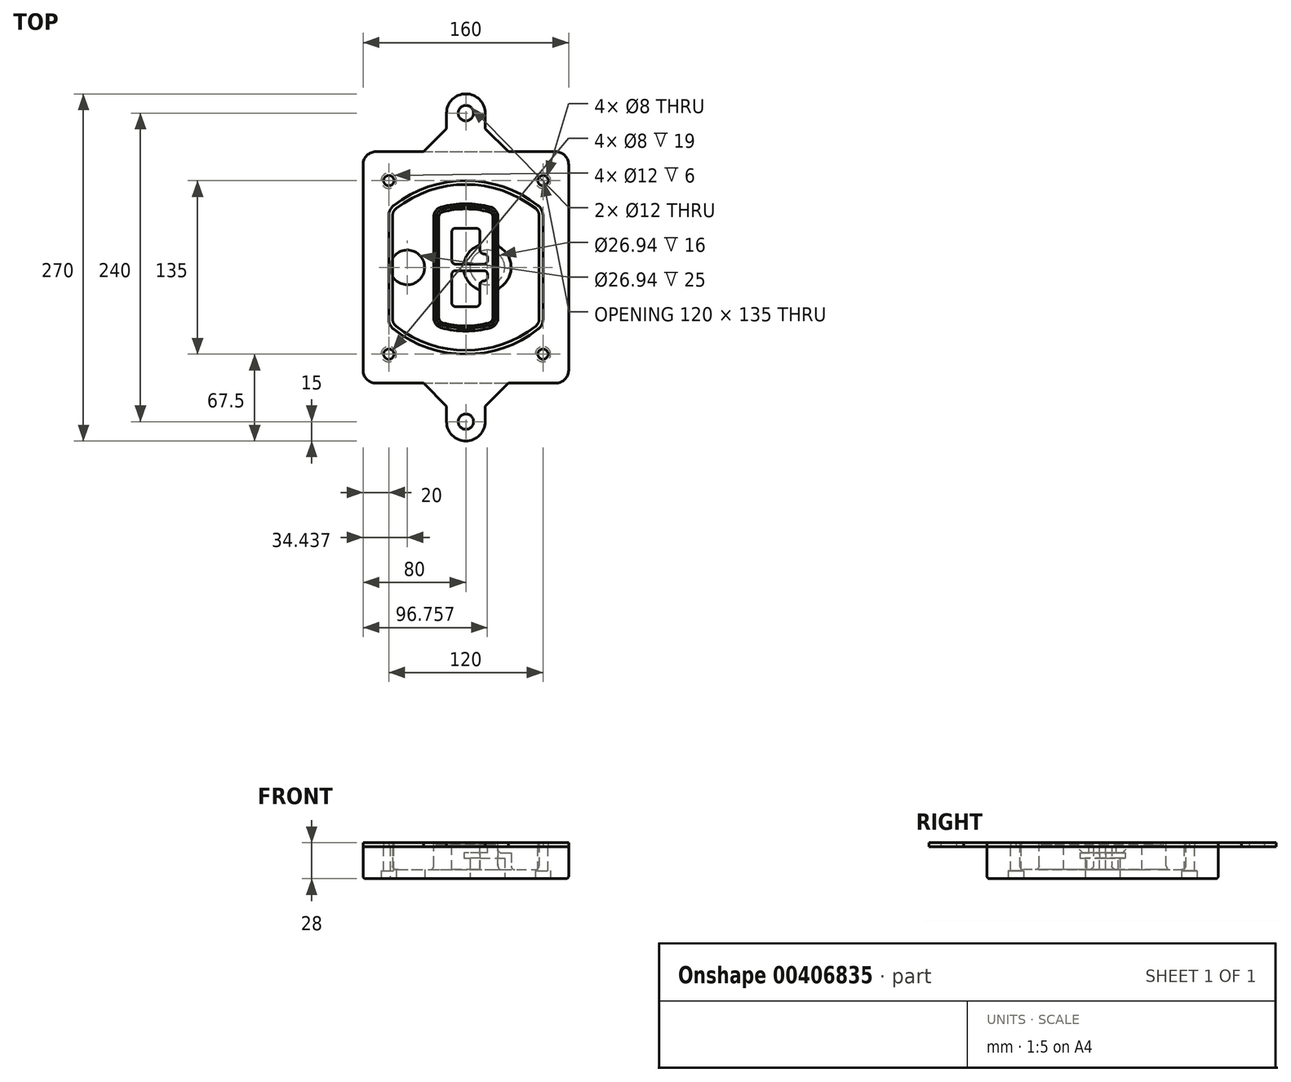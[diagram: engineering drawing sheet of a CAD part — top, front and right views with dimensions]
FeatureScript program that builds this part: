
annotation { "Feature Type Name" : "Feature", "Feature Type Description" : "" }
export const myFeature = defineFeature(function(context is Context, id is Id, definition is map)
    precondition{}
    {
        {
            var Q0;
            Q0=qCreatedBy(makeId("Top.planeOp"),FACE);
            var sketch = newSketch(context, id + "F0", { "sketchPlane" : qUnion([Q0])});
            skPoint(sketch, "E0.rect.middle", {"position": v(0, 0) * mm});
            skLineSegment(sketch, "E1.bottom", {"start": v(-70, -90) * mm, "end": v(70, -90) * mm});
            skLineSegment(sketch, "E1.top", {"start": v(-70, 90) * mm, "end": v(70, 90) * mm});
            skLineSegment(sketch, "E1.left", {"start": v(-80, -80) * mm, "end": v(-80, 80) * mm});
            skLineSegment(sketch, "E1.right", {"start": v(80, -80) * mm, "end": v(80, 80) * mm});
            skLineSegment(sketch, "E2", {"start": v(-80, 90) * mm, "end": v(80, -90) * mm, "construction": true});
            skLineSegment(sketch, "E3", {"start": v(80, 90) * mm, "end": v(-80, -90) * mm, "construction": true});
            skCircle(sketch, "E4", {"center": v(-60, 67.5) * mm, "radius": 4 * mm});
            skCircle(sketch, "E5", {"center": v(60, 67.5) * mm, "radius": 4 * mm});
            skCircle(sketch, "E6", {"center": v(60, -67.5) * mm, "radius": 4 * mm});
            skCircle(sketch, "E7", {"center": v(-60, -67.5) * mm, "radius": 4 * mm});
            skLineSegment(sketch, "E8", {"start": v(-60, 67.5) * mm, "end": v(60, 67.5) * mm, "construction": true});
            skLineSegment(sketch, "E9", {"start": v(60, 67.5) * mm, "end": v(60, -67.5) * mm, "construction": true});
            skLineSegment(sketch, "E10", {"start": v(60, -67.5) * mm, "end": v(-60, -67.5) * mm, "construction": true});
            skLineSegment(sketch, "E11", {"start": v(-60, -67.5) * mm, "end": v(-60, 67.5) * mm, "construction": true});
            skLineSegment(sketch, "E12", {"start": v(-60, 40.3) * mm, "end": v(-60, -40.3) * mm});
            skLineSegment(sketch, "E13", {"start": v(60, 40.3) * mm, "end": v(60, -40.3) * mm});
            skArc(sketch, "E14", {"start": v(56.15, 48.18) * mm, "mid": v(0, 67.5) * mm, "end": v(-56.15, 48.18) * mm});
            skArc(sketch, "E15", {"start": v(-56.15, -48.18) * mm, "mid": v(0, -67.5) * mm, "end": v(56.15, -48.18) * mm});
            skLineSegment(sketch, "E16", {"start": v(-60, 0) * mm, "end": v(60, 0) * mm, "construction": true});
            skPoint(sketch, "E17.visualSharp", {"position": v(-60, -45) * mm});
            skArc(sketch, "E17.filletArc", {"start": v(-60, -40.3) * mm, "mid": v(-58.99, -44.68) * mm, "end": v(-56.15, -48.18) * mm});
            skPoint(sketch, "E18.visualSharp", {"position": v(-60, 45) * mm});
            skArc(sketch, "E18.filletArc", {"start": v(-56.15, 48.18) * mm, "mid": v(-58.99, 44.68) * mm, "end": v(-60, 40.3) * mm});
            skPoint(sketch, "E19.visualSharp", {"position": v(60, 45) * mm});
            skArc(sketch, "E19.filletArc", {"start": v(60, 40.3) * mm, "mid": v(58.99, 44.68) * mm, "end": v(56.15, 48.18) * mm});
            skPoint(sketch, "E20.visualSharp", {"position": v(60, -45) * mm});
            skArc(sketch, "E20.filletArc", {"start": v(56.15, -48.18) * mm, "mid": v(58.99, -44.68) * mm, "end": v(60, -40.3) * mm});
            skPoint(sketch, "E21.visualSharp", {"position": v(-80, 90) * mm});
            skArc(sketch, "E21.filletArc", {"start": v(-70, 90) * mm, "mid": v(-77.07, 87.07) * mm, "end": v(-80, 80) * mm});
            skPoint(sketch, "E22.visualSharp", {"position": v(80, 90) * mm});
            skArc(sketch, "E22.filletArc", {"start": v(80, 80) * mm, "mid": v(77.07, 87.07) * mm, "end": v(70, 90) * mm});
            skPoint(sketch, "E23.visualSharp", {"position": v(80, -90) * mm});
            skArc(sketch, "E23.filletArc", {"start": v(70, -90) * mm, "mid": v(77.07, -87.07) * mm, "end": v(80, -80) * mm});
            skPoint(sketch, "E24.visualSharp", {"position": v(-80, -90) * mm});
            skArc(sketch, "E24.filletArc", {"start": v(-80, -80) * mm, "mid": v(-77.07, -87.07) * mm, "end": v(-70, -90) * mm});
            skArc(sketch, "E25.0", {"start": v(57, 40.3) * mm, "mid": v(56.3, 43.36) * mm, "end": v(54.3, 45.81) * mm});
            skLineSegment(sketch, "E25.1", {"start": v(57, 40.3) * mm, "end": v(57, -40.3) * mm});
            skArc(sketch, "E25.2", {"start": v(54.3, -45.81) * mm, "mid": v(56.3, -43.36) * mm, "end": v(57, -40.3) * mm});
            skArc(sketch, "E25.3", {"start": v(-54.3, -45.81) * mm, "mid": v(0, -64.5) * mm, "end": v(54.3, -45.81) * mm});
            skArc(sketch, "E25.4", {"start": v(-57, -40.3) * mm, "mid": v(-56.3, -43.36) * mm, "end": v(-54.3, -45.81) * mm});
            skArc(sketch, "E25.5", {"start": v(54.3, 45.81) * mm, "mid": v(0, 64.5) * mm, "end": v(-54.3, 45.81) * mm});
            skLineSegment(sketch, "E25.6", {"start": v(-57, 40.3) * mm, "end": v(-57, -40.3) * mm});
            skArc(sketch, "E25.7", {"start": v(-54.3, 45.81) * mm, "mid": v(-56.3, 43.36) * mm, "end": v(-57, 40.3) * mm});
            skArc(sketch, "E26.0", {"start": v(-58.62, 51.33) * mm, "mid": v(-62.58, 46.43) * mm, "end": v(-64, 40.3) * mm});
            skArc(sketch, "E26.1", {"start": v(58.62, 51.33) * mm, "mid": v(0, 71.5) * mm, "end": v(-58.62, 51.33) * mm});
            skArc(sketch, "E26.2", {"start": v(64, 40.3) * mm, "mid": v(62.58, 46.43) * mm, "end": v(58.62, 51.33) * mm});
            skLineSegment(sketch, "E26.3", {"start": v(64, 40.3) * mm, "end": v(64, -40.3) * mm});
            skArc(sketch, "E26.4", {"start": v(58.62, -51.33) * mm, "mid": v(62.58, -46.43) * mm, "end": v(64, -40.3) * mm});
            skLineSegment(sketch, "E26.5", {"start": v(-64, 40.3) * mm, "end": v(-64, -40.3) * mm});
            skArc(sketch, "E26.6", {"start": v(-58.62, -51.33) * mm, "mid": v(0, -71.5) * mm, "end": v(58.62, -51.33) * mm});
            skArc(sketch, "E26.7", {"start": v(-64, -40.3) * mm, "mid": v(-62.58, -46.43) * mm, "end": v(-58.62, -51.33) * mm});
            skSolve(sketch);
        }
        {
            var Q0;
            Q0=makeQuery(id+"F0.imprint","IMPRINT",FACE,{"disambiguationData":[TD([[makeQuery(id+"F0.imprint","IMPRINT",EDGE,{"derivedFrom":sQuery(id+"F0.wireOp",EDGE,"E1.bottom")}),1.0]])]});
            var Q1;
            Q1=makeQuery(id+"F0.imprint","IMPRINT",FACE,{"disambiguationData":[TD([[makeQuery(id+"F0.imprint","IMPRINT",EDGE,{"derivedFrom":sQuery(id+"F0.wireOp",EDGE,"E12")}),1.0]])]});
            var Q2;
            Q2=makeQuery(id+"F0.imprint","IMPRINT",FACE,{"disambiguationData":[TD([[makeQuery(id+"F0.imprint","IMPRINT",EDGE,{"derivedFrom":sQuery(id+"F0.wireOp",EDGE,"E25.0")}),1.0]])]});
            var Q3;
            Q3=makeQuery(id+"F0.imprint","IMPRINT",FACE,{"disambiguationData":[TD([[makeQuery(id+"F0.imprint","IMPRINT",EDGE,{"derivedFrom":sQuery(id+"F0.wireOp",EDGE,"E12")}),-1.0]])]});
            extrude(context, id + "F1", {"entities" : qUnion([Q0, Q1, Q2, Q3]), "oppositeDirection" : true, "depth" : 25 * mm});
        }
        {
            var Q0;
            Q0=makeQuery(id+"F0.imprint","IMPRINT",FACE,{"disambiguationData":[TD([[makeQuery(id+"F0.imprint","IMPRINT",EDGE,{"derivedFrom":sQuery(id+"F0.wireOp",EDGE,"E12")}),1.0]])]});
            extrude(context, id + "F2", {"entities" : qUnion([Q0]), "operationType" : NewBodyOperationType.ADD, "depth" : 3 * mm});
        }
        {
            var Q0;
            Q0=makeQuery(id+"F0.imprint","IMPRINT",FACE,{"disambiguationData":[TD([[makeQuery(id+"F0.imprint","IMPRINT",EDGE,{"derivedFrom":sQuery(id+"F0.wireOp",EDGE,"E25.0")}),1.0]])]});
            extrude(context, id + "F3", {"entities" : qUnion([Q0]), "operationType" : NewBodyOperationType.REMOVE, "oppositeDirection" : true, "depth" : 18 * mm});
        }
        {
            var Q0;
            Q0=makeQuery(id+"F2.opExtrude","CAP_FACE",FACE,{"disambiguationData":[OSD([sQuery(id+"F0.wireOp",EDGE,"E12"),sQuery(id+"F0.wireOp",EDGE,"E13"),sQuery(id+"F0.wireOp",EDGE,"E14"),sQuery(id+"F0.wireOp",EDGE,"E15"),sQuery(id+"F0.wireOp",EDGE,"E17.filletArc"),sQuery(id+"F0.wireOp",EDGE,"E18.filletArc"),sQuery(id+"F0.wireOp",EDGE,"E19.filletArc"),sQuery(id+"F0.wireOp",EDGE,"E20.filletArc"),sQuery(id+"F0.wireOp",EDGE,"E25.0"),sQuery(id+"F0.wireOp",EDGE,"E25.1"),sQuery(id+"F0.wireOp",EDGE,"E25.2"),sQuery(id+"F0.wireOp",EDGE,"E25.3"),sQuery(id+"F0.wireOp",EDGE,"E25.4"),sQuery(id+"F0.wireOp",EDGE,"E25.5"),sQuery(id+"F0.wireOp",EDGE,"E25.6"),sQuery(id+"F0.wireOp",EDGE,"E25.7")])],"isStart":false});
            var sketch = newSketch(context, id + "F4", { "sketchPlane" : qUnion([Q0])});
            skArc(sketch, "E27.0", {"start": v(-19.08, -46.97) * mm, "mid": v(0, -49.5) * mm, "end": v(19.08, -46.97) * mm});
            skArc(sketch, "E28.0", {"start": v(19.08, 46.97) * mm, "mid": v(0, 49.5) * mm, "end": v(-19.08, 46.97) * mm});
            skLineSegment(sketch, "E29", {"start": v(-25, 39.25) * mm, "end": v(-25, -39.25) * mm});
            skLineSegment(sketch, "E30", {"start": v(25, 39.25) * mm, "end": v(25, -39.25) * mm});
            skLineSegment(sketch, "E31", {"start": v(-25, 45.1) * mm, "end": v(25, 45.1) * mm, "construction": true});
            skLineSegment(sketch, "E32", {"start": v(-25, -45.1) * mm, "end": v(25, -45.1) * mm, "construction": true});
            skPoint(sketch, "E33.visualSharp", {"position": v(-25, 45.1) * mm});
            skArc(sketch, "E33.filletArc", {"start": v(-19.08, 46.97) * mm, "mid": v(-23.35, 44.11) * mm, "end": v(-25, 39.25) * mm});
            skPoint(sketch, "E34.visualSharp", {"position": v(25, 45.1) * mm});
            skArc(sketch, "E34.filletArc", {"start": v(25, 39.25) * mm, "mid": v(23.35, 44.11) * mm, "end": v(19.08, 46.97) * mm});
            skPoint(sketch, "E35.visualSharp", {"position": v(25, -45.1) * mm});
            skArc(sketch, "E35.filletArc", {"start": v(19.08, -46.97) * mm, "mid": v(23.35, -44.11) * mm, "end": v(25, -39.25) * mm});
            skPoint(sketch, "E36.visualSharp", {"position": v(-25, -45.1) * mm});
            skArc(sketch, "E36.filletArc", {"start": v(-25, -39.25) * mm, "mid": v(-23.35, -44.11) * mm, "end": v(-19.08, -46.97) * mm});
            skArc(sketch, "E37.0", {"start": v(54.3, 45.81) * mm, "mid": v(0, 64.5) * mm, "end": v(-54.3, 45.81) * mm});
            skArc(sketch, "E37.1", {"start": v(-54.3, 45.81) * mm, "mid": v(-56.3, 43.36) * mm, "end": v(-57, 40.3) * mm});
            skLineSegment(sketch, "E37.2", {"start": v(-57, 40.3) * mm, "end": v(-57, -40.3) * mm});
            skArc(sketch, "E37.3", {"start": v(-57, -40.3) * mm, "mid": v(-56.3, -43.36) * mm, "end": v(-54.3, -45.81) * mm});
            skArc(sketch, "E37.4", {"start": v(-54.3, -45.81) * mm, "mid": v(0, -64.5) * mm, "end": v(54.3, -45.81) * mm});
            skArc(sketch, "E37.5", {"start": v(54.3, -45.81) * mm, "mid": v(56.3, -43.36) * mm, "end": v(57, -40.3) * mm});
            skLineSegment(sketch, "E37.6", {"start": v(57, 40.3) * mm, "end": v(57, -40.3) * mm});
            skArc(sketch, "E37.7", {"start": v(57, 40.3) * mm, "mid": v(56.3, 43.36) * mm, "end": v(54.3, 45.81) * mm});
            skLineSegment(sketch, "E38.0", {"start": v(23, 39.25) * mm, "end": v(23, -39.25) * mm});
            skArc(sketch, "E38.1", {"start": v(18.56, -45.04) * mm, "mid": v(21.76, -42.9) * mm, "end": v(23, -39.25) * mm});
            skArc(sketch, "E38.2", {"start": v(-18.56, -45.04) * mm, "mid": v(0, -47.5) * mm, "end": v(18.56, -45.04) * mm});
            skArc(sketch, "E38.3", {"start": v(-23, -39.25) * mm, "mid": v(-21.76, -42.9) * mm, "end": v(-18.56, -45.04) * mm});
            skLineSegment(sketch, "E38.4", {"start": v(-23, 39.25) * mm, "end": v(-23, -39.25) * mm});
            skArc(sketch, "E38.5", {"start": v(23, 39.25) * mm, "mid": v(21.76, 42.9) * mm, "end": v(18.56, 45.04) * mm});
            skArc(sketch, "E38.6", {"start": v(-18.56, 45.04) * mm, "mid": v(-21.76, 42.9) * mm, "end": v(-23, 39.25) * mm});
            skArc(sketch, "E38.7", {"start": v(18.56, 45.04) * mm, "mid": v(0, 47.5) * mm, "end": v(-18.56, 45.04) * mm});
            skArc(sketch, "E39.0", {"start": v(21, 39.25) * mm, "mid": v(20.18, 41.68) * mm, "end": v(18.04, 43.1) * mm});
            skLineSegment(sketch, "E39.1", {"start": v(21, 39.25) * mm, "end": v(21, -39.25) * mm});
            skArc(sketch, "E39.2", {"start": v(18.04, -43.1) * mm, "mid": v(20.18, -41.68) * mm, "end": v(21, -39.25) * mm});
            skArc(sketch, "E39.3", {"start": v(-18.04, -43.1) * mm, "mid": v(0, -45.5) * mm, "end": v(18.04, -43.1) * mm});
            skArc(sketch, "E39.4", {"start": v(-21, -39.25) * mm, "mid": v(-20.18, -41.68) * mm, "end": v(-18.04, -43.1) * mm});
            skArc(sketch, "E39.5", {"start": v(18.04, 43.1) * mm, "mid": v(0, 45.5) * mm, "end": v(-18.04, 43.1) * mm});
            skLineSegment(sketch, "E39.6", {"start": v(-21, 39.25) * mm, "end": v(-21, -39.25) * mm});
            skArc(sketch, "E39.7", {"start": v(-18.04, 43.1) * mm, "mid": v(-20.18, 41.68) * mm, "end": v(-21, 39.25) * mm});
            skLineSegment(sketch, "E40", {"start": v(-25, 0) * mm, "end": v(25, 0) * mm, "construction": true});
            skLineSegment(sketch, "E41", {"start": v(-11, 5.5) * mm, "end": v(-11, 27.5) * mm});
            skLineSegment(sketch, "E42", {"start": v(-8, 30.5) * mm, "end": v(8, 30.5) * mm});
            skLineSegment(sketch, "E43", {"start": v(11, 27.5) * mm, "end": v(11, 13.5) * mm});
            skLineSegment(sketch, "E44", {"start": v(14, 10.5) * mm, "end": v(14, 10.5) * mm});
            skLineSegment(sketch, "E45", {"start": v(17, 7.5) * mm, "end": v(17, 5.5) * mm});
            skLineSegment(sketch, "E46", {"start": v(14, 2.5) * mm, "end": v(-8, 2.5) * mm});
            skPoint(sketch, "E47.visualSharp", {"position": v(-11, 30.5) * mm});
            skArc(sketch, "E47.filletArc", {"start": v(-8, 30.5) * mm, "mid": v(-10.12, 29.62) * mm, "end": v(-11, 27.5) * mm});
            skPoint(sketch, "E48.visualSharp", {"position": v(11, 30.5) * mm});
            skArc(sketch, "E48.filletArc", {"start": v(11, 27.5) * mm, "mid": v(10.12, 29.62) * mm, "end": v(8, 30.5) * mm});
            skPoint(sketch, "E49.visualSharp", {"position": v(11, 10.5) * mm});
            skArc(sketch, "E49.filletArc", {"start": v(11, 13.5) * mm, "mid": v(11.88, 11.38) * mm, "end": v(14, 10.5) * mm});
            skPoint(sketch, "E50.visualSharp", {"position": v(17, 10.5) * mm});
            skArc(sketch, "E50.filletArc", {"start": v(17, 7.5) * mm, "mid": v(16.12, 9.62) * mm, "end": v(14, 10.5) * mm});
            skPoint(sketch, "E51.visualSharp", {"position": v(17, 2.5) * mm});
            skArc(sketch, "E51.filletArc", {"start": v(14, 2.5) * mm, "mid": v(16.12, 3.38) * mm, "end": v(17, 5.5) * mm});
            skPoint(sketch, "E52.visualSharp", {"position": v(-11, 2.5) * mm});
            skArc(sketch, "E52.filletArc", {"start": v(-11, 5.5) * mm, "mid": v(-10.12, 3.38) * mm, "end": v(-8, 2.5) * mm});
            skLineSegment(sketch, "E53.0.MirrorCS", {"start": v(14, -2.5) * mm, "end": v(-8, -2.5) * mm});
            skArc(sketch, "E54.0.MirrorCS", {"start": v(-11, -5.5) * mm, "mid": v(-10.12, -3.38) * mm, "end": v(-8, -2.5) * mm});
            skLineSegment(sketch, "E55.0.MirrorCS", {"start": v(-11, -5.5) * mm, "end": v(-11, -27.5) * mm});
            skArc(sketch, "E56.0.MirrorCS", {"start": v(-8, -30.5) * mm, "mid": v(-10.12, -29.62) * mm, "end": v(-11, -27.5) * mm});
            skLineSegment(sketch, "E57.0.MirrorCS", {"start": v(-8, -30.5) * mm, "end": v(8, -30.5) * mm});
            skArc(sketch, "E58.0.MirrorCS", {"start": v(11, -27.5) * mm, "mid": v(10.12, -29.62) * mm, "end": v(8, -30.5) * mm});
            skLineSegment(sketch, "E59.0.MirrorCS", {"start": v(11, -27.5) * mm, "end": v(11, -13.5) * mm});
            skArc(sketch, "E60.0.MirrorCS", {"start": v(11, -13.5) * mm, "mid": v(11.88, -11.38) * mm, "end": v(14, -10.5) * mm});
            skArc(sketch, "E61.0.MirrorCS", {"start": v(17, -7.5) * mm, "mid": v(16.12, -9.62) * mm, "end": v(14, -10.5) * mm});
            skLineSegment(sketch, "E62.0.MirrorCS", {"start": v(17, -7.5) * mm, "end": v(17, -5.5) * mm});
            skArc(sketch, "E63.0.MirrorCS", {"start": v(14, -2.5) * mm, "mid": v(16.12, -3.38) * mm, "end": v(17, -5.5) * mm});
            skSolve(sketch);
        }
        {
            var Q0;
            Q0=makeQuery(id+"F4.imprint","IMPRINT",FACE,{"disambiguationData":[TD([[makeQuery(id+"F4.imprint","IMPRINT",EDGE,{"derivedFrom":sQuery(id+"F4.wireOp",EDGE,"E27.0")}),1.0]])]});
            var Q1;
            Q1=makeQuery(id+"F4.imprint","IMPRINT",FACE,{"disambiguationData":[TD([[makeQuery(id+"F4.imprint","IMPRINT",EDGE,{"derivedFrom":sQuery(id+"F4.wireOp",EDGE,"E38.0")}),-1.0]])]});
            var Q2;
            Q2=makeQuery(id+"F4.imprint","IMPRINT",FACE,{"disambiguationData":[TD([[makeQuery(id+"F4.imprint","IMPRINT",EDGE,{"derivedFrom":sQuery(id+"F4.wireOp",EDGE,"E39.0")}),1.0]])]});
            extrude(context, id + "F5", {"entities" : qUnion([Q0, Q1, Q2]), "operationType" : NewBodyOperationType.ADD, "endBound" : BoundingType.UP_TO_NEXT, "oppositeDirection" : true, "depth" : 25 * mm});
        }
        {
            var Q0;
            Q0=makeQuery(id+"F4.imprint","IMPRINT",FACE,{"disambiguationData":[TD([[makeQuery(id+"F4.imprint","IMPRINT",EDGE,{"derivedFrom":sQuery(id+"F4.wireOp",EDGE,"E38.0")}),-1.0]])]});
            extrude(context, id + "F6", {"entities" : qUnion([Q0]), "operationType" : NewBodyOperationType.REMOVE, "oppositeDirection" : true, "depth" : 2 * mm});
        }
        {
            var Q0;
            Q0=makeQuery(id+"F1.opExtrude","CAP_FACE",FACE,{"disambiguationData":[OSD([sQuery(id+"F0.wireOp",EDGE,"E1.bottom"),sQuery(id+"F0.wireOp",EDGE,"E1.top"),sQuery(id+"F0.wireOp",EDGE,"E1.left"),sQuery(id+"F0.wireOp",EDGE,"E1.right"),sQuery(id+"F0.wireOp",EDGE,"E4"),sQuery(id+"F0.wireOp",EDGE,"E5"),sQuery(id+"F0.wireOp",EDGE,"E6"),sQuery(id+"F0.wireOp",EDGE,"E7"),sQuery(id+"F0.wireOp",EDGE,"E21.filletArc"),sQuery(id+"F0.wireOp",EDGE,"E22.filletArc"),sQuery(id+"F0.wireOp",EDGE,"E23.filletArc"),sQuery(id+"F0.wireOp",EDGE,"E24.filletArc")])],"isStart":false});
            var sketch = newSketch(context, id + "F7", { "sketchPlane" : qUnion([Q0])});
            skCircle(sketch, "E64", {"center": v(16.76, 0) * mm, "radius": 13.47 * mm});
            skCircle(sketch, "E65", {"center": v(-45.56, 0) * mm, "radius": 13.47 * mm});
            skLineSegment(sketch, "E66", {"start": v(80, 0) * mm, "end": v(-80, 0) * mm});
            skCircle(sketch, "E67", {"center": v(16.76, 0) * mm, "radius": 18.47 * mm});
            skCircle(sketch, "E68", {"center": v(60, -67.5) * mm, "radius": 6 * mm});
            skCircle(sketch, "E69", {"center": v(-60, -67.5) * mm, "radius": 6 * mm});
            skCircle(sketch, "E70", {"center": v(-60, 67.5) * mm, "radius": 6 * mm});
            skCircle(sketch, "E71", {"center": v(60, 67.5) * mm, "radius": 6 * mm});
            skSolve(sketch);
        }
        {
            var Q0;
            {var subQ1=sQuery(id+"F7.wireOp",EDGE,"E66");var subQ4=sQuery(id+"F7.wireOp",EDGE,"E64");var subQ6=makeQuery(id+"F7.imprint","INTERSECT",VERTEX,{"disambiguationData":[OD(0.0)],"derivedFrom":[subQ4,subQ1]});Q0=makeQuery(id+"F7.imprint","IMPRINT",FACE,{"disambiguationData":[TD([[makeQuery(id+"F7.imprint","IMPRINT",EDGE,{"disambiguationData":[TD([[subQ6,-1.0]])],"derivedFrom":subQ4}),-1.0]])]});}
            var Q1;
            {var subQ0=sQuery(id+"F7.wireOp",EDGE,"E66");var subQ1=sQuery(id+"F7.wireOp",EDGE,"E64");var subQ3=makeQuery(id+"F7.imprint","INTERSECT",VERTEX,{"disambiguationData":[OD(0.0)],"derivedFrom":[subQ1,subQ0]});Q1=makeQuery(id+"F7.imprint","IMPRINT",FACE,{"disambiguationData":[TD([[makeQuery(id+"F7.imprint","IMPRINT",EDGE,{"disambiguationData":[TD([[subQ3,-1.0]])],"derivedFrom":subQ1}),1.0]])]});}
            var Q2;
            {var subQ0=sQuery(id+"F7.wireOp",EDGE,"E66");var subQ1=sQuery(id+"F7.wireOp",EDGE,"E64");var subQ3=makeQuery(id+"F7.imprint","INTERSECT",VERTEX,{"disambiguationData":[OD(0.0)],"derivedFrom":[subQ1,subQ0]});Q2=makeQuery(id+"F7.imprint","IMPRINT",FACE,{"disambiguationData":[TD([[makeQuery(id+"F7.imprint","IMPRINT",EDGE,{"disambiguationData":[TD([[subQ3,1.0]])],"derivedFrom":subQ1}),1.0]])]});}
            var Q3;
            {var subQ1=sQuery(id+"F7.wireOp",EDGE,"E66");var subQ4=sQuery(id+"F7.wireOp",EDGE,"E64");var subQ6=makeQuery(id+"F7.imprint","INTERSECT",VERTEX,{"disambiguationData":[OD(0.0)],"derivedFrom":[subQ4,subQ1]});Q3=makeQuery(id+"F7.imprint","IMPRINT",FACE,{"disambiguationData":[TD([[makeQuery(id+"F7.imprint","IMPRINT",EDGE,{"disambiguationData":[TD([[subQ6,1.0]])],"derivedFrom":subQ4}),-1.0]])]});}
            extrude(context, id + "F8", {"entities" : qUnion([Q0, Q1, Q2, Q3]), "operationType" : NewBodyOperationType.ADD, "oppositeDirection" : true, "depth" : 20 * mm});
        }
        {
            var Q0;
            {var subQ0=sQuery(id+"F7.wireOp",EDGE,"E66");var subQ1=sQuery(id+"F7.wireOp",EDGE,"E64");var subQ3=makeQuery(id+"F7.imprint","INTERSECT",VERTEX,{"disambiguationData":[OD(0.0)],"derivedFrom":[subQ1,subQ0]});Q0=makeQuery(id+"F7.imprint","IMPRINT",FACE,{"disambiguationData":[TD([[makeQuery(id+"F7.imprint","IMPRINT",EDGE,{"disambiguationData":[TD([[subQ3,-1.0]])],"derivedFrom":subQ1}),1.0]])]});}
            var Q1;
            {var subQ0=sQuery(id+"F7.wireOp",EDGE,"E66");var subQ1=sQuery(id+"F7.wireOp",EDGE,"E64");var subQ3=makeQuery(id+"F7.imprint","INTERSECT",VERTEX,{"disambiguationData":[OD(0.0)],"derivedFrom":[subQ1,subQ0]});Q1=makeQuery(id+"F7.imprint","IMPRINT",FACE,{"disambiguationData":[TD([[makeQuery(id+"F7.imprint","IMPRINT",EDGE,{"disambiguationData":[TD([[subQ3,1.0]])],"derivedFrom":subQ1}),1.0]])]});}
            extrude(context, id + "F9", {"entities" : qUnion([Q0, Q1]), "operationType" : NewBodyOperationType.REMOVE, "oppositeDirection" : true, "depth" : 16 * mm});
        }
        {
            var Q0;
            {var subQ0=sQuery(id+"F7.wireOp",EDGE,"E66");var subQ1=sQuery(id+"F7.wireOp",EDGE,"E65");var subQ3=makeQuery(id+"F7.imprint","INTERSECT",VERTEX,{"disambiguationData":[OD(0.0)],"derivedFrom":[subQ1,subQ0]});Q0=makeQuery(id+"F7.imprint","IMPRINT",FACE,{"disambiguationData":[TD([[makeQuery(id+"F7.imprint","IMPRINT",EDGE,{"disambiguationData":[TD([[subQ3,-1.0]])],"derivedFrom":subQ1}),1.0]])]});}
            var Q1;
            {var subQ0=sQuery(id+"F7.wireOp",EDGE,"E66");var subQ1=sQuery(id+"F7.wireOp",EDGE,"E65");var subQ3=makeQuery(id+"F7.imprint","INTERSECT",VERTEX,{"disambiguationData":[OD(0.0)],"derivedFrom":[subQ1,subQ0]});Q1=makeQuery(id+"F7.imprint","IMPRINT",FACE,{"disambiguationData":[TD([[makeQuery(id+"F7.imprint","IMPRINT",EDGE,{"disambiguationData":[TD([[subQ3,1.0]])],"derivedFrom":subQ1}),1.0]])]});}
            extrude(context, id + "F10", {"entities" : qUnion([Q0, Q1]), "operationType" : NewBodyOperationType.REMOVE, "oppositeDirection" : true, "depth" : 25 * mm});
        }
        {
            var Q0;
            Q0=makeQuery(id+"F7.imprint","IMPRINT",FACE,{"disambiguationData":[TD([[makeQuery(id+"F7.imprint","IMPRINT",EDGE,{"derivedFrom":sQuery(id+"F7.wireOp",EDGE,"E68")}),1.0]])]});
            var Q1;
            Q1=makeQuery(id+"F7.imprint","IMPRINT",FACE,{"disambiguationData":[TD([[makeQuery(id+"F7.imprint","IMPRINT",EDGE,{"derivedFrom":makeQuery(id+"F1.opExtrude","CAP_EDGE",EDGE,{"disambiguationData":[OSD([sQuery(id+"F0.wireOp",EDGE,"E5")])],"isStart":false})}),-1.0]])]});
            var Q2;
            Q2=makeQuery(id+"F7.imprint","IMPRINT",FACE,{"disambiguationData":[TD([[makeQuery(id+"F7.imprint","IMPRINT",EDGE,{"derivedFrom":sQuery(id+"F7.wireOp",EDGE,"E69")}),1.0]])]});
            var Q3;
            Q3=makeQuery(id+"F7.imprint","IMPRINT",FACE,{"disambiguationData":[TD([[makeQuery(id+"F7.imprint","IMPRINT",EDGE,{"derivedFrom":makeQuery(id+"F1.opExtrude","CAP_EDGE",EDGE,{"disambiguationData":[OSD([sQuery(id+"F0.wireOp",EDGE,"E4")])],"isStart":false})}),-1.0]])]});
            var Q4;
            Q4=makeQuery(id+"F7.imprint","IMPRINT",FACE,{"disambiguationData":[TD([[makeQuery(id+"F7.imprint","IMPRINT",EDGE,{"derivedFrom":sQuery(id+"F7.wireOp",EDGE,"E70")}),1.0]])]});
            var Q5;
            Q5=makeQuery(id+"F7.imprint","IMPRINT",FACE,{"disambiguationData":[TD([[makeQuery(id+"F7.imprint","IMPRINT",EDGE,{"derivedFrom":makeQuery(id+"F1.opExtrude","CAP_EDGE",EDGE,{"disambiguationData":[OSD([sQuery(id+"F0.wireOp",EDGE,"E7")])],"isStart":false})}),-1.0]])]});
            var Q6;
            Q6=makeQuery(id+"F7.imprint","IMPRINT",FACE,{"disambiguationData":[TD([[makeQuery(id+"F7.imprint","IMPRINT",EDGE,{"derivedFrom":sQuery(id+"F7.wireOp",EDGE,"E71")}),1.0]])]});
            var Q7;
            Q7=makeQuery(id+"F7.imprint","IMPRINT",FACE,{"disambiguationData":[TD([[makeQuery(id+"F7.imprint","IMPRINT",EDGE,{"derivedFrom":makeQuery(id+"F1.opExtrude","CAP_EDGE",EDGE,{"disambiguationData":[OSD([sQuery(id+"F0.wireOp",EDGE,"E6")])],"isStart":false})}),-1.0]])]});
            extrude(context, id + "F11", {"entities" : qUnion([Q0, Q1, Q2, Q3, Q4, Q5, Q6, Q7]), "operationType" : NewBodyOperationType.REMOVE, "oppositeDirection" : true, "depth" : 6 * mm});
        }
        {
            var Q0;
            Q0=makeQuery(id+"F9.boolean.opBoolean","COPY",FACE,{"derivedFrom":makeQuery(id+"F9.opExtrude","CAP_FACE",FACE,{"disambiguationData":[OSD([sQuery(id+"F7.wireOp",EDGE,"E64")])],"isStart":false})});
            var sketch = newSketch(context, id + "F12", { "sketchPlane" : qUnion([Q0])});
            skArc(sketch, "E72.0", {"start": v(11, 17.55) * mm, "mid": v(2.57, 11.82) * mm, "end": v(-1.54, 2.5) * mm});
            skArc(sketch, "E72.1", {"start": v(-1.54, -2.5) * mm, "mid": v(2.57, -11.82) * mm, "end": v(11, -17.55) * mm});
            skLineSegment(sketch, "E73", {"start": v(-1.54, -2.5) * mm, "end": v(14, -2.5) * mm});
            skLineSegment(sketch, "E74.0", {"start": v(14, 2.5) * mm, "end": v(-1.54, 2.5) * mm});
            skArc(sketch, "E74.1", {"start": v(14, 2.5) * mm, "mid": v(16.12, 3.38) * mm, "end": v(17, 5.5) * mm});
            skLineSegment(sketch, "E74.2", {"start": v(17, 7.5) * mm, "end": v(17, 5.5) * mm});
            skArc(sketch, "E74.3", {"start": v(17, 7.5) * mm, "mid": v(16.12, 9.62) * mm, "end": v(14, 10.5) * mm});
            skArc(sketch, "E74.4", {"start": v(11, 13.5) * mm, "mid": v(11.88, 11.38) * mm, "end": v(14, 10.5) * mm});
            skLineSegment(sketch, "E74.5", {"start": v(11, 17.55) * mm, "end": v(11, 13.5) * mm});
            skLineSegment(sketch, "E74.7", {"start": v(14, -2.5) * mm, "end": v(-1.54, -2.5) * mm});
            skArc(sketch, "E74.8", {"start": v(14, -2.5) * mm, "mid": v(16.12, -3.38) * mm, "end": v(17, -5.5) * mm});
            skLineSegment(sketch, "E74.9", {"start": v(17, -7.5) * mm, "end": v(17, -5.5) * mm});
            skArc(sketch, "E74.10", {"start": v(17, -7.5) * mm, "mid": v(16.12, -9.62) * mm, "end": v(14, -10.5) * mm});
            skArc(sketch, "E74.11", {"start": v(11, -13.5) * mm, "mid": v(11.88, -11.38) * mm, "end": v(14, -10.5) * mm});
            skLineSegment(sketch, "E74.12", {"start": v(11, -17.55) * mm, "end": v(11, -13.5) * mm});
            skPoint(sketch, "E75.orphan", {"position": v(11, -27.5) * mm});
            skPoint(sketch, "E76.orphan", {"position": v(-8, -2.5) * mm});
            skPoint(sketch, "E77.orphan", {"position": v(-8, 2.5) * mm});
            skPoint(sketch, "E78.orphan", {"position": v(11, 27.5) * mm});
            skSolve(sketch);
        }
        {
            var Q0;
            {var subQ7=sQuery(id+"F12.wireOp",EDGE,"E72.0");var subQ14=sQuery(id+"F12.wireOp",EDGE,"E72.1");var subQ16=sQuery(id+"F12.wireOp",EDGE,"E74.1");var subQ18=sQuery(id+"F12.wireOp",EDGE,"E74.8");Q0=qUnion([makeQuery(id+"F12.imprint","IMPRINT",FACE,{"disambiguationData":[TD([[makeQuery(id+"F12.imprint","IMPRINT",EDGE,{"derivedFrom":subQ7}),1.0]])]}),makeQuery(id+"F12.imprint","IMPRINT",FACE,{"disambiguationData":[TD([[makeQuery(id+"F12.imprint","IMPRINT",EDGE,{"derivedFrom":subQ14}),1.0]])]}),makeQuery(id+"F12.imprint","IMPRINT",FACE,{"disambiguationData":[TD([[makeQuery(id+"F12.imprint","IMPRINT",EDGE,{"derivedFrom":subQ16}),1.0]])]}),makeQuery(id+"F12.imprint","IMPRINT",FACE,{"disambiguationData":[TD([[makeQuery(id+"F12.imprint","IMPRINT",EDGE,{"derivedFrom":subQ18}),-1.0]])]})]);}
            var Q1;
            Q1=makeQuery(id+"F5.boolean.opBoolean","SPLIT",FACE,{"disambiguationData":[TD([makeQuery(id+"F5.opExtrude","SWEPT_FACE",FACE,{"disambiguationData":[OSD([sQuery(id+"F4.wireOp",EDGE,"E41")])]})])],"derivedFrom":makeQuery(id+"F3.boolean.opBoolean","COPY",FACE,{"derivedFrom":makeQuery(id+"F3.opExtrude","CAP_FACE",FACE,{"disambiguationData":[OSD([sQuery(id+"F0.wireOp",EDGE,"E25.0"),sQuery(id+"F0.wireOp",EDGE,"E25.1"),sQuery(id+"F0.wireOp",EDGE,"E25.2"),sQuery(id+"F0.wireOp",EDGE,"E25.3"),sQuery(id+"F0.wireOp",EDGE,"E25.4"),sQuery(id+"F0.wireOp",EDGE,"E25.5"),sQuery(id+"F0.wireOp",EDGE,"E25.6"),sQuery(id+"F0.wireOp",EDGE,"E25.7")])],"isStart":false})})});
            extrude(context, id + "F13", {"entities" : qUnion([Q0]), "operationType" : NewBodyOperationType.REMOVE, "endBound" : BoundingType.UP_TO_SURFACE, "endBoundEntityFace" : qUnion([Q1]), "depth" : 25 * mm});
        }
        {
            var Q0;
            Q0=makeQuery(id+"F3.boolean.opBoolean","COPY",EDGE,{"derivedFrom":makeQuery(id+"F3.opExtrude","CAP_EDGE",EDGE,{"disambiguationData":[OSD([sQuery(id+"F0.wireOp",EDGE,"E25.6")])],"isStart":false})});
            var Q1;
            Q1=makeQuery(id+"F8.boolean.opBoolean","INTERSECT",EDGE,{"derivedFrom":[makeQuery(id+"F5.opExtrude","SWEPT_FACE",FACE,{"disambiguationData":[OSD([sQuery(id+"F4.wireOp",EDGE,"E30")])]}),makeQuery(id+"F8.opExtrude","CAP_FACE",FACE,{"disambiguationData":[OSD([sQuery(id+"F7.wireOp",EDGE,"E67")])],"isStart":false})]});
            var Q2;
            Q2=makeQuery(id+"F8.boolean.opBoolean","INTERSECT",EDGE,{"disambiguationData":[OD(1.0)],"derivedFrom":[makeQuery(id+"F5.opExtrude","SWEPT_FACE",FACE,{"disambiguationData":[OSD([sQuery(id+"F4.wireOp",EDGE,"E30")])]}),makeQuery(id+"F8.opExtrude","SWEPT_FACE",FACE,{"disambiguationData":[OSD([sQuery(id+"F7.wireOp",EDGE,"E67")])]})]});
            var Q3;
            {var subQ0=sQuery(id+"F4.wireOp",EDGE,"E30");Q3=makeQuery(id+"F8.boolean.opBoolean","SPLIT",EDGE,{"disambiguationData":[TD([makeQuery(id+"F5.opExtrude","SWEPT_FACE",FACE,{"disambiguationData":[OSD([sQuery(id+"F4.wireOp",EDGE,"E35.filletArc")])]})])],"derivedFrom":makeQuery(id+"F5.opExtrude","CAP_EDGE",EDGE,{"disambiguationData":[OSD([subQ0])],"isStart":false})});}
            var Q4;
            {var subQ0=sQuery(id+"F0.wireOp",EDGE,"E25.7");var subQ1=sQuery(id+"F0.wireOp",EDGE,"E25.1");var subQ2=sQuery(id+"F0.wireOp",EDGE,"E25.6");var subQ3=sQuery(id+"F0.wireOp",EDGE,"E25.5");var subQ4=sQuery(id+"F0.wireOp",EDGE,"E25.4");var subQ5=sQuery(id+"F0.wireOp",EDGE,"E25.0");var subQ6=sQuery(id+"F0.wireOp",EDGE,"E25.2");var subQ7=sQuery(id+"F0.wireOp",EDGE,"E25.3");Q4=makeQuery(id+"F8.boolean.opBoolean","INTERSECT",EDGE,{"derivedFrom":[makeQuery(id+"F5.boolean.opBoolean","SPLIT",FACE,{"disambiguationData":[TD([makeQuery(id+"F2.opExtrude","SWEPT_FACE",FACE,{"disambiguationData":[OSD([subQ5])]})])],"derivedFrom":makeQuery(id+"F3.boolean.opBoolean","COPY",FACE,{"derivedFrom":makeQuery(id+"F3.opExtrude","CAP_FACE",FACE,{"disambiguationData":[OSD([subQ5,subQ1,subQ6,subQ7,subQ4,subQ3,subQ2,subQ0])],"isStart":false})})}),makeQuery(id+"F8.opExtrude","SWEPT_FACE",FACE,{"disambiguationData":[OSD([sQuery(id+"F7.wireOp",EDGE,"E67")])]})]});}
            var Q5;
            Q5=makeQuery(id+"F8.boolean.opBoolean","INTERSECT",EDGE,{"disambiguationData":[OD(0.0)],"derivedFrom":[makeQuery(id+"F5.opExtrude","SWEPT_FACE",FACE,{"disambiguationData":[OSD([sQuery(id+"F4.wireOp",EDGE,"E30")])]}),makeQuery(id+"F8.opExtrude","SWEPT_FACE",FACE,{"disambiguationData":[OSD([sQuery(id+"F7.wireOp",EDGE,"E67")])]})]});
            fillet(context, id + "F14", {"entities" : qUnion([Q0, Q1, Q2, Q3, Q4, Q5]), "radius" : 3 * mm, "tangentPropagation" : true, "allowEdgeOverflow" : false});
        }
        {
            var Q0;
            Q0=makeQuery(id+"F1.opExtrude","CAP_EDGE",EDGE,{"disambiguationData":[OSD([sQuery(id+"F0.wireOp",EDGE,"E1.bottom")])],"isStart":false});
            fillet(context, id + "F15", {"entities" : qUnion([Q0]), "radius" : 2 * mm, "tangentPropagation" : true, "allowEdgeOverflow" : false});
        }
        {
            var Q0;
            {var subQ0=sQuery(id+"F0.wireOp",EDGE,"E21.filletArc");var subQ1=sQuery(id+"F0.wireOp",EDGE,"E7");var subQ2=sQuery(id+"F0.wireOp",EDGE,"E6");var subQ3=sQuery(id+"F0.wireOp",EDGE,"E5");var subQ4=sQuery(id+"F0.wireOp",EDGE,"E4");var subQ5=sQuery(id+"F0.wireOp",EDGE,"E22.filletArc");var subQ6=sQuery(id+"F0.wireOp",EDGE,"E1.bottom");var subQ7=sQuery(id+"F0.wireOp",EDGE,"E1.right");var subQ8=sQuery(id+"F0.wireOp",EDGE,"E1.top");var subQ9=sQuery(id+"F0.wireOp",EDGE,"E1.left");var subQ10=sQuery(id+"F0.wireOp",EDGE,"E23.filletArc");var subQ11=sQuery(id+"F0.wireOp",EDGE,"E24.filletArc");Q0=makeQuery(id+"F2.boolean.opBoolean","SPLIT",FACE,{"disambiguationData":[TD([makeQuery(id+"F1.opExtrude","SWEPT_FACE",FACE,{"disambiguationData":[OSD([subQ6])]})])],"derivedFrom":makeQuery(id+"F1.opExtrude","CAP_FACE",FACE,{"disambiguationData":[OSD([subQ6,subQ8,subQ9,subQ7,subQ4,subQ3,subQ2,subQ1,subQ0,subQ5,subQ10,subQ11])],"isStart":true})});}
            var sketch = newSketch(context, id + "F16", { "sketchPlane" : qUnion([Q0])});
            skLineSegment(sketch, "E79", {"start": v(0, 90) * mm, "end": v(0, 120) * mm, "construction": true});
            skPoint(sketch, "E79.endSnap0", {"position": v(0, 90) * mm});
            skCircle(sketch, "E80", {"center": v(0, 120) * mm, "radius": 6 * mm});
            skLineSegment(sketch, "E81", {"start": v(-33, 90) * mm, "end": v(-15, 108) * mm});
            skLineSegment(sketch, "E82", {"start": v(-15, 108) * mm, "end": v(-15, 120) * mm});
            skArc(sketch, "E83", {"start": v(-15, 120) * mm, "mid": v(0, 135) * mm, "end": v(15, 120) * mm});
            skLineSegment(sketch, "E84", {"start": v(15, 120) * mm, "end": v(15, 108) * mm});
            skLineSegment(sketch, "E85", {"start": v(15, 108) * mm, "end": v(33, 90) * mm});
            skLineSegment(sketch, "E86", {"start": v(-15, 108) * mm, "end": v(-15, 90) * mm, "construction": true});
            skPoint(sketch, "E87", {"position": v(-80, 0) * mm});
            skPoint(sketch, "E88", {"position": v(80, 0) * mm});
            skLineSegment(sketch, "E89", {"start": v(-80, 0) * mm, "end": v(80, 0) * mm, "construction": true});
            skLineSegment(sketch, "E90.MirrorCS", {"start": v(15, -108) * mm, "end": v(33, -90) * mm});
            skLineSegment(sketch, "E91.MirrorCS", {"start": v(-33, -90) * mm, "end": v(-15, -108) * mm});
            skLineSegment(sketch, "E92.MirrorCS", {"start": v(-15, -108) * mm, "end": v(-15, -120) * mm});
            skArc(sketch, "E93.MirrorCS", {"start": v(-15, -120) * mm, "mid": v(0, -135) * mm, "end": v(15, -120) * mm});
            skLineSegment(sketch, "E94.MirrorCS", {"start": v(15, -120) * mm, "end": v(15, -108) * mm});
            skCircle(sketch, "E95.MirrorC", {"center": v(0, -120) * mm, "radius": 6 * mm});
            skSolve(sketch);
        }
        {
            var Q0;
            {var subQ1=sQuery(id+"F16.wireOp",EDGE,"E90.MirrorCS");Q0=makeQuery(id+"F16.imprint","IMPRINT",FACE,{"disambiguationData":[TD([[makeQuery(id+"F16.imprint","IMPRINT",EDGE,{"derivedFrom":subQ1}),1.0]])]});}
            var Q1;
            Q1=makeQuery(id+"F16.imprint","IMPRINT",FACE,{"disambiguationData":[TD([[makeQuery(id+"F16.imprint","IMPRINT",EDGE,{"derivedFrom":makeQuery(id+"F1.opExtrude","CAP_EDGE",EDGE,{"disambiguationData":[OSD([sQuery(id+"F0.wireOp",EDGE,"E1.left")])],"isStart":true})}),-1.0]])]});
            var Q2;
            Q2=makeQuery(id+"F16.imprint","IMPRINT",FACE,{"disambiguationData":[TD([[makeQuery(id+"F16.imprint","IMPRINT",EDGE,{"derivedFrom":sQuery(id+"F16.wireOp",EDGE,"E80")}),-1.0]])]});
            var Q3;
            Q3=makeQuery(id+"F2.opExtrude","CAP_FACE",FACE,{"disambiguationData":[OSD([sQuery(id+"F0.wireOp",EDGE,"E12"),sQuery(id+"F0.wireOp",EDGE,"E13"),sQuery(id+"F0.wireOp",EDGE,"E14"),sQuery(id+"F0.wireOp",EDGE,"E15"),sQuery(id+"F0.wireOp",EDGE,"E17.filletArc"),sQuery(id+"F0.wireOp",EDGE,"E18.filletArc"),sQuery(id+"F0.wireOp",EDGE,"E19.filletArc"),sQuery(id+"F0.wireOp",EDGE,"E20.filletArc"),sQuery(id+"F0.wireOp",EDGE,"E25.0"),sQuery(id+"F0.wireOp",EDGE,"E25.1"),sQuery(id+"F0.wireOp",EDGE,"E25.2"),sQuery(id+"F0.wireOp",EDGE,"E25.3"),sQuery(id+"F0.wireOp",EDGE,"E25.4"),sQuery(id+"F0.wireOp",EDGE,"E25.5"),sQuery(id+"F0.wireOp",EDGE,"E25.6"),sQuery(id+"F0.wireOp",EDGE,"E25.7")])],"isStart":false});
            extrude(context, id + "F17", {"entities" : qUnion([Q0, Q1, Q2]), "endBound" : BoundingType.UP_TO_SURFACE, "endBoundEntityFace" : qUnion([Q3]), "depth" : 1 * mm});
        }
    });
